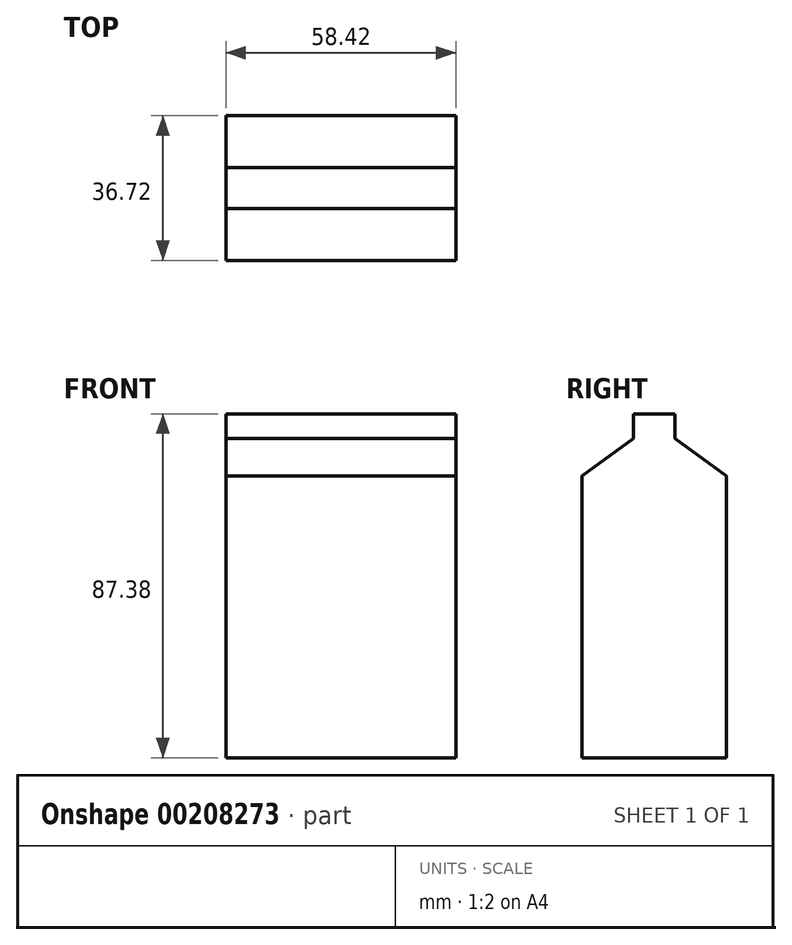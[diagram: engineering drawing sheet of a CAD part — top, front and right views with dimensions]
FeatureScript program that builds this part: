
annotation { "Feature Type Name" : "Feature", "Feature Type Description" : "" }
export const myFeature = defineFeature(function(context is Context, id is Id, definition is map)
    precondition{}
    {
        {
            var Q0;
            Q0=qCreatedBy(makeId("Right.planeOp"),FACE);
            var sketch = newSketch(context, id + "F0", { "sketchPlane" : qUnion([Q0])});
            skLineSegment(sketch, "E0.bottom", {"start": v(18.36, -35.82) * mm, "end": v(-18.36, -35.82) * mm});
            skLineSegment(sketch, "E0.top", {"start": v(18.36, 35.82) * mm, "end": v(-18.36, 35.82) * mm});
            skLineSegment(sketch, "E0.left", {"start": v(18.36, -35.82) * mm, "end": v(18.36, 35.82) * mm});
            skLineSegment(sketch, "E0.right", {"start": v(-18.36, -35.82) * mm, "end": v(-18.36, 35.82) * mm});
            skPoint(sketch, "E0.middle", {"position": v(0, 0) * mm});
            skLineSegment(sketch, "E1", {"start": v(-18.36, 35.82) * mm, "end": v(-5.25, 45.3) * mm});
            skLineSegment(sketch, "E2", {"start": v(-5.25, 45.3) * mm, "end": v(-5.25, 51.56) * mm});
            skLineSegment(sketch, "E3", {"start": v(-5.25, 51.56) * mm, "end": v(0, 51.56) * mm});
            skLineSegment(sketch, "E4.MirrorCS", {"start": v(5.25, 51.56) * mm, "end": v(0, 51.56) * mm});
            skLineSegment(sketch, "E5.MirrorCS", {"start": v(5.25, 45.3) * mm, "end": v(5.25, 51.56) * mm});
            skLineSegment(sketch, "E6.MirrorCS", {"start": v(18.36, 35.82) * mm, "end": v(5.25, 45.3) * mm});
            skSolve(sketch);
        }
        {
            var Q0;
            Q0=makeQuery(id+"F0.imprint","IMPRINT",FACE,{"disambiguationData":[TD([[makeQuery(id+"F0.imprint","IMPRINT",EDGE,{"derivedFrom":sQuery(id+"F0.wireOp",EDGE,"E0.bottom")}),-1.0]])]});
            var Q1;
            Q1=makeQuery(id+"F0.imprint","IMPRINT",FACE,{"disambiguationData":[TD([[makeQuery(id+"F0.imprint","IMPRINT",EDGE,{"derivedFrom":sQuery(id+"F0.wireOp",EDGE,"E0.top")}),-1.0]])]});
            extrude(context, id + "F1", {"entities" : qUnion([Q0, Q1]), "endBound" : BoundingType.SYMMETRIC, "depth" : 58.42 * mm});
        }
    });
